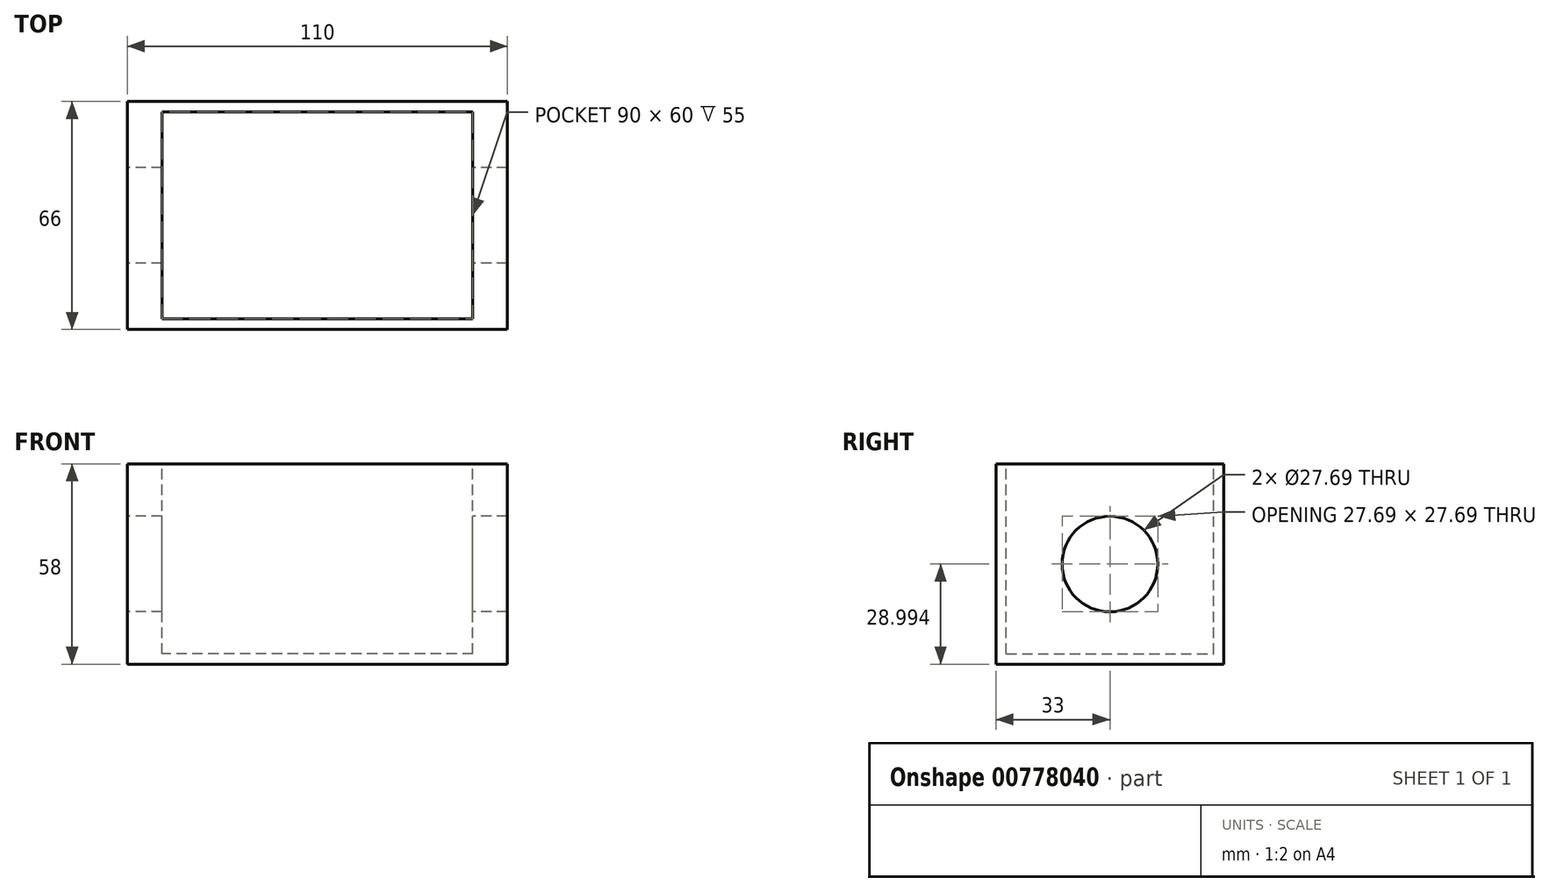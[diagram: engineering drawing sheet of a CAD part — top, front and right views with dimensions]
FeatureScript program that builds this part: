
annotation { "Feature Type Name" : "Feature", "Feature Type Description" : "" }
export const myFeature = defineFeature(function(context is Context, id is Id, definition is map)
    precondition{}
    {
        {
            var Q0;
            Q0=qCreatedBy(makeId("Top.planeOp"),FACE);
            var sketch = newSketch(context, id + "F0", { "sketchPlane" : qUnion([Q0])});
            skLineSegment(sketch, "E0.bottom", {"start": v(55, -33) * mm, "end": v(-55, -33) * mm});
            skLineSegment(sketch, "E0.top", {"start": v(55, 33) * mm, "end": v(-55, 33) * mm});
            skLineSegment(sketch, "E0.left", {"start": v(55, -33) * mm, "end": v(55, 33) * mm});
            skLineSegment(sketch, "E0.right", {"start": v(-55, -33) * mm, "end": v(-55, 33) * mm});
            skPoint(sketch, "E0.middle", {"position": v(0, 0) * mm});
            skSolve(sketch);
        }
        {
            var Q0;
            Q0=makeQuery(id+"F0.imprint","IMPRINT",FACE,{"disambiguationData":[TD([[makeQuery(id+"F0.imprint","IMPRINT",EDGE,{"derivedFrom":sQuery(id+"F0.wireOp",EDGE,"E0.bottom")}),-1.0]])]});
            extrude(context, id + "F1", {"entities" : qUnion([Q0]), "depth" : 58 * mm, "offsetDistance" : 25 * mm});
        }
        {
            var Q0;
            Q0=makeQuery(id+"F1.opExtrude","CAP_FACE",FACE,{"disambiguationData":[OSD([sQuery(id+"F0.wireOp",EDGE,"E0.bottom"),sQuery(id+"F0.wireOp",EDGE,"E0.top"),sQuery(id+"F0.wireOp",EDGE,"E0.left"),sQuery(id+"F0.wireOp",EDGE,"E0.right")])],"isStart":false});
            var sketch = newSketch(context, id + "F2", { "sketchPlane" : qUnion([Q0])});
            skLineSegment(sketch, "E1.bottom", {"start": v(45, -30) * mm, "end": v(-45, -30) * mm});
            skLineSegment(sketch, "E1.top", {"start": v(45, 30) * mm, "end": v(-45, 30) * mm});
            skLineSegment(sketch, "E1.left", {"start": v(45, -30) * mm, "end": v(45, 30) * mm});
            skLineSegment(sketch, "E1.right", {"start": v(-45, -30) * mm, "end": v(-45, 30) * mm});
            skPoint(sketch, "E1.middle", {"position": v(0, 0) * mm});
            skSolve(sketch);
        }
        {
            var Q0;
            Q0=makeQuery(id+"F2.imprint","IMPRINT",FACE,{"disambiguationData":[TD([[makeQuery(id+"F2.imprint","IMPRINT",EDGE,{"derivedFrom":sQuery(id+"F2.wireOp",EDGE,"E1.bottom")}),-1.0]])]});
            extrude(context, id + "F3", {"entities" : qUnion([Q0]), "operationType" : NewBodyOperationType.REMOVE, "oppositeDirection" : true, "depth" : 55 * mm, "offsetDistance" : 25 * mm});
        }
        {
            var Q0;
            Q0=makeQuery(id+"F1.opExtrude","SWEPT_FACE",FACE,{"disambiguationData":[OSD([sQuery(id+"F0.wireOp",EDGE,"E0.right")])]});
            var sketch = newSketch(context, id + "F4", { "sketchPlane" : qUnion([Q0])});
            skLineSegment(sketch, "E2", {"start": v(-33, 29) * mm, "end": v(33, 29) * mm, "construction": true});
            skSolve(sketch);
        }
        {
            var Q0;
            {var subQ0=sQuery(id+"F0.wireOp",EDGE,"E0.right");Q0=makeQuery(id+"F4.imprint","IMPRINT",FACE,{"disambiguationData":[TD([[makeQuery(id+"F4.imprint","IMPRINT",EDGE,{"derivedFrom":makeQuery(id+"F1.opExtrude","CAP_EDGE",EDGE,{"disambiguationData":[OSD([subQ0])],"isStart":true})}),-1.0]])]});}
            var sketch = newSketch(context, id + "F5", { "sketchPlane" : qUnion([Q0])});
            skCircle(sketch, "E3", {"center": v(0, 29) * mm, "radius": 13.84 * mm});
            skSolve(sketch);
        }
        {
            var Q0;
            Q0 = qSketchRegion(id + "F5", true);
            extrude(context, id + "F6", {"entities" : qUnion([Q0]), "operationType" : NewBodyOperationType.REMOVE, "oppositeDirection" : true, "depth" : 115 * mm, "offsetDistance" : 25 * mm});
        }
    });
